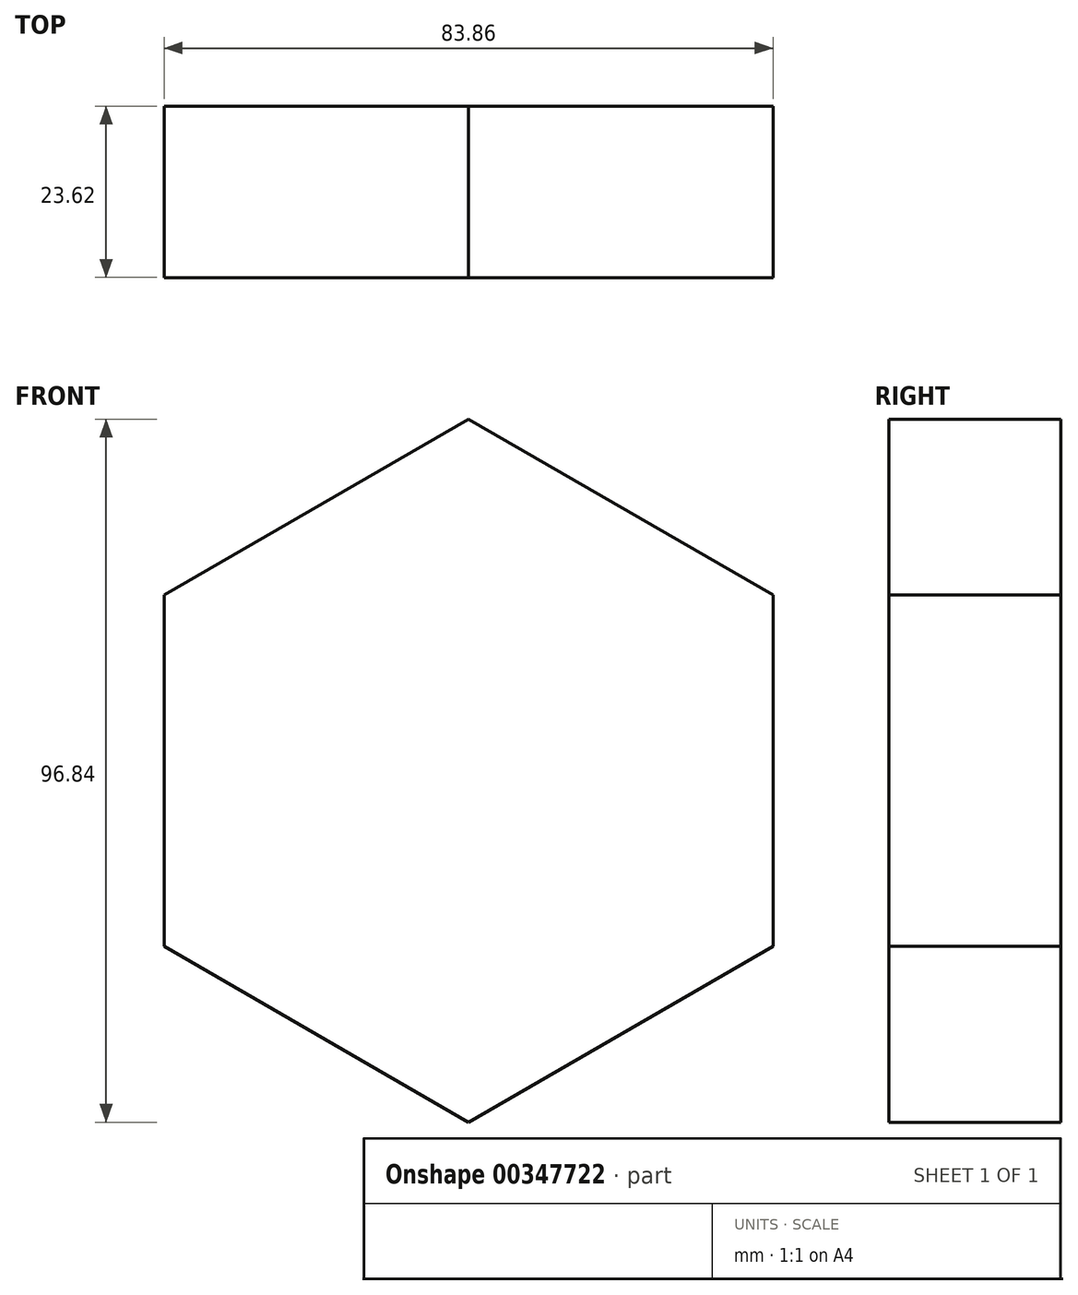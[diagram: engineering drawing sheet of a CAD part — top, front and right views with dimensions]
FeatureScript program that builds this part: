
annotation { "Feature Type Name" : "Feature", "Feature Type Description" : "" }
export const myFeature = defineFeature(function(context is Context, id is Id, definition is map)
    precondition{}
    {
        {
            var Q0;
            Q0=qCreatedBy(makeId("Front.planeOp"),FACE);
            var sketch = newSketch(context, id + "F0", { "sketchPlane" : qUnion([Q0])});
            skCircle(sketch, "E0.cCircle", {"center": v(0, 0) * mm, "radius": 41.93 * mm, "construction": true});
            skLineSegment(sketch, "E0.0", {"start": v(41.93, 24.21) * mm, "end": v(41.93, -24.21) * mm});
            skLineSegment(sketch, "E0.1", {"start": v(41.93, -24.21) * mm, "end": v(0, -48.42) * mm});
            skLineSegment(sketch, "E0.2", {"start": v(0, -48.42) * mm, "end": v(-41.93, -24.21) * mm});
            skLineSegment(sketch, "E0.3", {"start": v(-41.93, -24.21) * mm, "end": v(-41.93, 24.21) * mm});
            skLineSegment(sketch, "E0.4", {"start": v(-41.93, 24.21) * mm, "end": v(0, 48.42) * mm});
            skLineSegment(sketch, "E0.5", {"start": v(0, 48.42) * mm, "end": v(41.93, 24.21) * mm});
            skPoint(sketch, "E0.0.midPoint", {"position": v(41.93, 0) * mm});
            skSolve(sketch);
        }
        {
            var Q0;
            Q0=makeQuery(id+"F0.imprint","IMPRINT",FACE,{"disambiguationData":[TD([[makeQuery(id+"F0.imprint","IMPRINT",EDGE,{"derivedFrom":sQuery(id+"F0.wireOp",EDGE,"E0.0")}),-1.0]])]});
            extrude(context, id + "F1", {"entities" : qUnion([Q0]), "depth" : 23.62 * mm});
        }
    });
